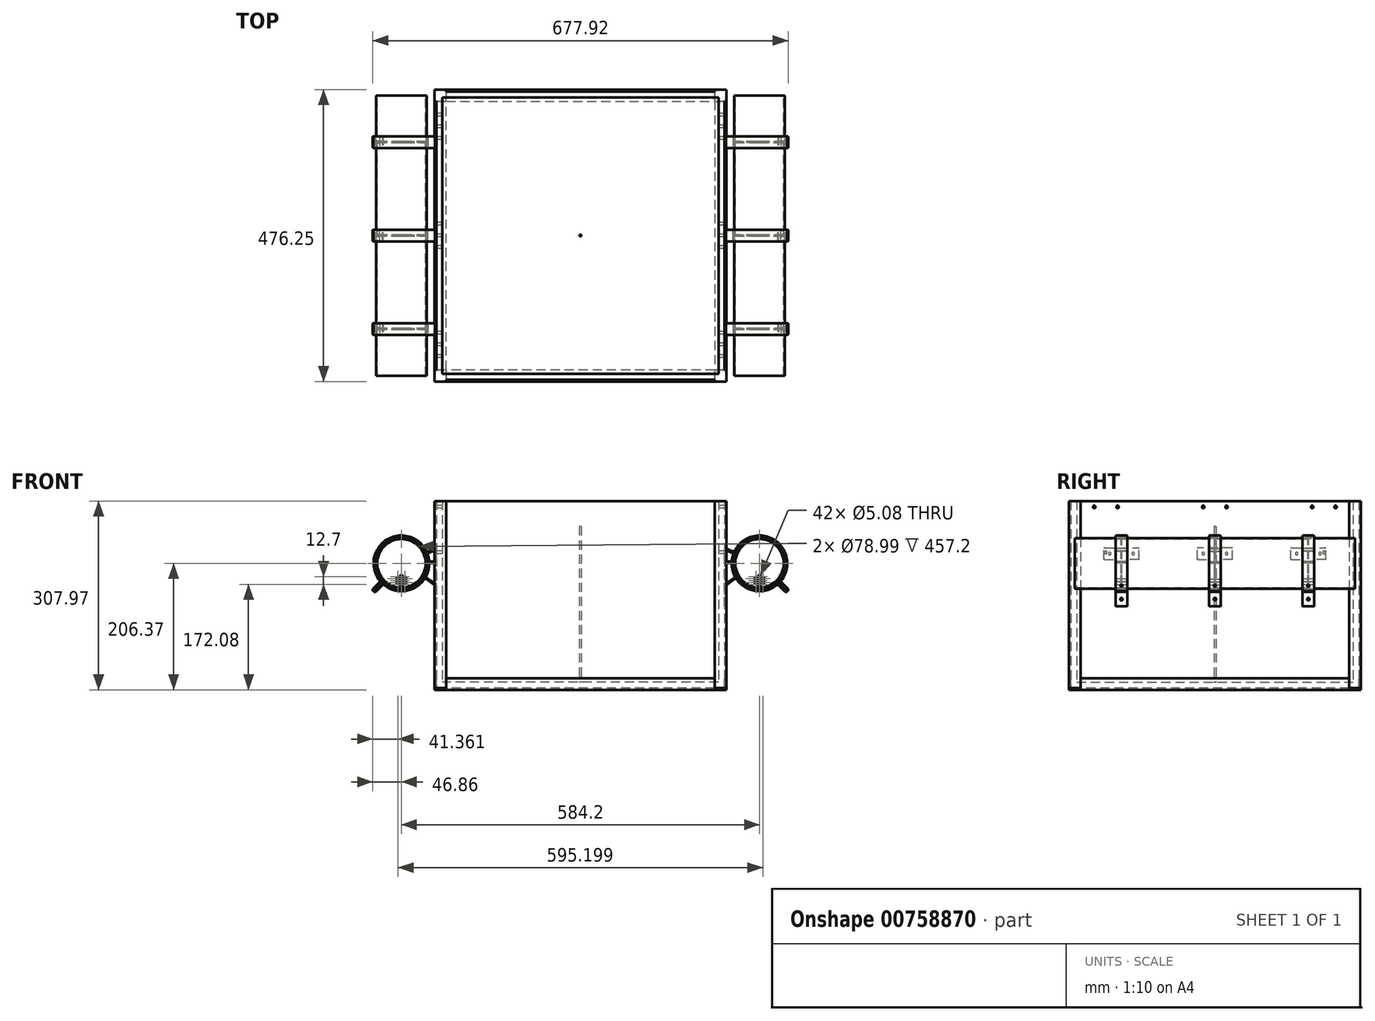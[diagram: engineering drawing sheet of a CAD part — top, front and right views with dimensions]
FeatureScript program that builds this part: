
annotation { "Feature Type Name" : "Feature", "Feature Type Description" : "" }
export const myFeature = defineFeature(function(context is Context, id is Id, definition is map)
    precondition{}
    {
        {
            var Q0;
            Q0=qCreatedBy(makeId("Top.planeOp"),FACE);
            var sketch = newSketch(context, id + "F0", { "sketchPlane" : qUnion([Q0])});
            skLineSegment(sketch, "E0.bottom", {"start": v(234.95, -234.95) * mm, "end": v(-234.95, -234.95) * mm});
            skLineSegment(sketch, "E0.top", {"start": v(234.95, 234.95) * mm, "end": v(-234.95, 234.95) * mm});
            skLineSegment(sketch, "E0.left", {"start": v(234.95, -234.95) * mm, "end": v(234.95, 234.95) * mm});
            skLineSegment(sketch, "E0.right", {"start": v(-234.95, -234.95) * mm, "end": v(-234.95, 234.95) * mm});
            skPoint(sketch, "E0.middle", {"position": v(0, 0) * mm});
            skLineSegment(sketch, "E1", {"start": v(-234.95, 238.13) * mm, "end": v(-238.13, 238.13) * mm});
            skLineSegment(sketch, "E2", {"start": v(-238.13, 238.13) * mm, "end": v(-238.13, 219.08) * mm});
            skLineSegment(sketch, "E3", {"start": v(-238.13, 219.08) * mm, "end": v(-234.95, 219.08) * mm});
            skLineSegment(sketch, "E4", {"start": v(-238.13, 238.13) * mm, "end": v(-219.08, 238.13) * mm});
            skLineSegment(sketch, "E5", {"start": v(-219.08, 238.13) * mm, "end": v(-219.08, 234.95) * mm});
            skLineSegment(sketch, "E6.1.0", {"start": v(-238.13, -238.13) * mm, "end": v(-238.13, -219.08) * mm});
            skLineSegment(sketch, "E6.1.1", {"start": v(-238.13, -238.13) * mm, "end": v(-219.08, -238.13) * mm});
            skLineSegment(sketch, "E6.1.2", {"start": v(-219.08, -238.13) * mm, "end": v(-219.08, -234.95) * mm});
            skLineSegment(sketch, "E6.1.3", {"start": v(-238.13, -219.08) * mm, "end": v(-234.95, -219.08) * mm});
            skLineSegment(sketch, "E6.1.4", {"start": v(-238.13, -234.95) * mm, "end": v(-238.13, -238.13) * mm});
            skLineSegment(sketch, "E6.2.0", {"start": v(238.13, -238.13) * mm, "end": v(219.08, -238.13) * mm});
            skLineSegment(sketch, "E6.2.1", {"start": v(238.13, -238.13) * mm, "end": v(238.13, -219.08) * mm});
            skLineSegment(sketch, "E6.2.2", {"start": v(238.13, -219.08) * mm, "end": v(234.95, -219.08) * mm});
            skLineSegment(sketch, "E6.2.3", {"start": v(219.08, -238.13) * mm, "end": v(219.08, -234.95) * mm});
            skLineSegment(sketch, "E6.2.4", {"start": v(234.95, -238.13) * mm, "end": v(238.13, -238.13) * mm});
            skLineSegment(sketch, "E6.3.0", {"start": v(238.13, 238.13) * mm, "end": v(238.13, 219.08) * mm});
            skLineSegment(sketch, "E6.3.1", {"start": v(238.13, 238.13) * mm, "end": v(219.08, 238.13) * mm});
            skLineSegment(sketch, "E6.3.2", {"start": v(219.08, 238.13) * mm, "end": v(219.08, 234.95) * mm});
            skLineSegment(sketch, "E6.3.3", {"start": v(238.13, 219.08) * mm, "end": v(234.95, 219.08) * mm});
            skLineSegment(sketch, "E6.3.4", {"start": v(238.13, 234.95) * mm, "end": v(238.13, 238.13) * mm});
            skLineSegment(sketch, "E7.0", {"start": v(225.43, 225.43) * mm, "end": v(-225.42, 225.42) * mm});
            skLineSegment(sketch, "E7.1", {"start": v(225.43, -225.42) * mm, "end": v(225.43, 225.42) * mm});
            skLineSegment(sketch, "E7.2", {"start": v(225.43, -225.42) * mm, "end": v(-225.43, -225.43) * mm});
            skLineSegment(sketch, "E7.3", {"start": v(-225.43, -225.43) * mm, "end": v(-225.42, 225.42) * mm});
            skSolve(sketch);
        }
        {
            var Q0;
            Q0=qSketchRegion(id+"F0",true);
            extrude(context, id + "F1", {"entities" : qUnion([Q0]), "depth" : 304.8 * mm, "offsetDistance" : 25.4 * mm});
        }
        {
            var Q0;
            Q0=makeQuery(id+"F0.imprint","IMPRINT",FACE,{"disambiguationData":[TD([[makeQuery(id+"F0.imprint","IMPRINT",EDGE,{"derivedFrom":sQuery(id+"F0.wireOp",EDGE,"E7.0")}),1.0]])]});
            extrude(context, id + "F2", {"entities" : qUnion([Q0]), "operationType" : NewBodyOperationType.ADD, "depth" : 9.52 * mm, "offsetDistance" : 25.4 * mm});
        }
        {
            var Q0;
            Q0=makeQuery(id+"F1.opExtrude","SWEPT_FACE",FACE,{"disambiguationData":[OSD([sQuery(id+"F0.wireOp",EDGE,"E0.right")])]});
            var sketch = newSketch(context, id + "F3", { "sketchPlane" : qUnion([Q0])});
            skLineSegment(sketch, "E8", {"start": v(0, 304.8) * mm, "end": v(0, 297.18) * mm});
            skLineSegment(sketch, "E9", {"start": v(0, 304.8) * mm, "end": v(-177.8, 304.8) * mm});
            skLineSegment(sketch, "E10", {"start": v(-177.8, 304.8) * mm, "end": v(-177.8, 297.18) * mm});
            skLineSegment(sketch, "E11", {"start": v(0, 297.18) * mm, "end": v(0, 220.98) * mm});
            skLineSegment(sketch, "E12", {"start": v(-177.8, 297.18) * mm, "end": v(-177.8, 220.98) * mm});
            skLineSegment(sketch, "E13.MirrorCS", {"start": v(177.8, 304.8) * mm, "end": v(177.8, 297.18) * mm});
            skLineSegment(sketch, "E14.MirrorCS", {"start": v(177.8, 297.18) * mm, "end": v(177.8, 220.98) * mm});
            skLineSegment(sketch, "E15.MirrorCS", {"start": v(0, 304.8) * mm, "end": v(177.8, 304.8) * mm});
            skLineSegment(sketch, "E16", {"start": v(-177.8, 304.8) * mm, "end": v(-177.8, 295.28) * mm});
            skLineSegment(sketch, "E17", {"start": v(-177.8, 295.28) * mm, "end": v(-158.75, 295.28) * mm});
            skLineSegment(sketch, "E18.MirrorCS", {"start": v(-177.8, 295.28) * mm, "end": v(-196.85, 295.28) * mm});
            skLineSegment(sketch, "E19", {"start": v(-88.9, 304.8) * mm, "end": v(-88.9, 246.4) * mm});
            skLineSegment(sketch, "E20.MirrorCS", {"start": v(0, 304.8) * mm, "end": v(0, 295.28) * mm});
            skLineSegment(sketch, "E21.MirrorCS", {"start": v(0, 295.28) * mm, "end": v(19.05, 295.28) * mm});
            skLineSegment(sketch, "E22.MirrorCS", {"start": v(0, 295.28) * mm, "end": v(-19.05, 295.28) * mm});
            skLineSegment(sketch, "E23.MirrorCS", {"start": v(177.8, 304.8) * mm, "end": v(177.8, 295.28) * mm});
            skLineSegment(sketch, "E24.MirrorCS", {"start": v(177.8, 295.28) * mm, "end": v(196.85, 295.28) * mm});
            skLineSegment(sketch, "E25.MirrorCS", {"start": v(177.8, 295.28) * mm, "end": v(158.75, 295.28) * mm});
            skSolve(sketch);
        }
        {
            var Q0;
            Q0=sQuery(id+"F3.wireOp",VERTEX,"E11.end");
            var Q1;
            Q1=sQuery(id+"F3.wireOp",VERTEX,"E14.MirrorCS.end");
            var Q2;
            Q2=sQuery(id+"F3.wireOp",VERTEX,"E17.end");
            var Q3;
            Q3=sQuery(id+"F3.wireOp",VERTEX,"E18.MirrorCS.end");
            var Q4;
            Q4=sQuery(id+"F3.wireOp",VERTEX,"E22.MirrorCS.end");
            var Q5;
            Q5=sQuery(id+"F3.wireOp",VERTEX,"E21.MirrorCS.end");
            var Q6;
            Q6=sQuery(id+"F3.wireOp",VERTEX,"E12.end");
            var Q7;
            Q7=sQuery(id+"F3.wireOp",VERTEX,"E24.MirrorCS.end");
            var Q8;
            Q8=sQuery(id+"F3.wireOp",VERTEX,"E25.MirrorCS.end");
            var Q9;
            Q9=makeQuery(id+"F1.opExtrude","SWEPT_BODY",BODY,{"disambiguationData":[OSD([sQuery(id+"F0.wireOp",EDGE,"E0.bottom"),sQuery(id+"F0.wireOp",EDGE,"E0.top"),sQuery(id+"F0.wireOp",EDGE,"E0.left"),sQuery(id+"F0.wireOp",EDGE,"E0.right"),sQuery(id+"F0.wireOp",EDGE,"E2"),sQuery(id+"F0.wireOp",EDGE,"E3"),sQuery(id+"F0.wireOp",EDGE,"E4"),sQuery(id+"F0.wireOp",EDGE,"E5"),sQuery(id+"F0.wireOp",EDGE,"E6.1.0"),sQuery(id+"F0.wireOp",EDGE,"E6.1.1"),sQuery(id+"F0.wireOp",EDGE,"E6.1.2"),sQuery(id+"F0.wireOp",EDGE,"E6.1.3"),sQuery(id+"F0.wireOp",EDGE,"E6.1.4"),sQuery(id+"F0.wireOp",EDGE,"E6.2.0"),sQuery(id+"F0.wireOp",EDGE,"E6.2.1"),sQuery(id+"F0.wireOp",EDGE,"E6.2.2"),sQuery(id+"F0.wireOp",EDGE,"E6.2.3"),sQuery(id+"F0.wireOp",EDGE,"E6.2.4"),sQuery(id+"F0.wireOp",EDGE,"E6.3.0"),sQuery(id+"F0.wireOp",EDGE,"E6.3.1"),sQuery(id+"F0.wireOp",EDGE,"E6.3.2"),sQuery(id+"F0.wireOp",EDGE,"E6.3.3"),sQuery(id+"F0.wireOp",EDGE,"E6.3.4"),sQuery(id+"F0.wireOp",EDGE,"E7.0"),sQuery(id+"F0.wireOp",EDGE,"E7.1"),sQuery(id+"F0.wireOp",EDGE,"E7.2"),sQuery(id+"F0.wireOp",EDGE,"E7.3")])]});
            hole(context, id + "F4", {"style" : HoleStyle.SIMPLE, "endStyle" : HoleEndStyle.BLIND, "standardTappedOrClearance" : lookupTablePath({ "standard" : "ANSI", "fit" : "Close", "size" : "#8", "type" : "Clearance" }), "standardBlindInLast" : lookupTablePath({ "fit" : "Close", "standard" : "ANSI", "size" : "#8", "type" : "Clearance" }), "holeDiameter" : 4.32 * mm, "holeDepth" : 762 * mm, "isTappedThrough" : true, "tappedDepth" : 12.7 * mm, "tapClearance" : 3, "locations" : qUnion([Q0, Q1, Q2, Q3, Q4, Q5, Q6, Q7, Q8]), "scope" : qUnion([Q9]), "majorDiameter" : 6.35 * mm});
        }
        {
            var Q0;
            Q0=makeQuery(id+"F1.opExtrude","SWEPT_FACE",FACE,{"disambiguationData":[OSD([sQuery(id+"F0.wireOp",EDGE,"E6.1.2")])]});
            var sketch = newSketch(context, id + "F5", { "sketchPlane" : qUnion([Q0])});
            skLineSegment(sketch, "E26", {"start": v(-238.12, -3.17) * mm, "end": v(-238.12, 15.87) * mm});
            skLineSegment(sketch, "E27", {"start": v(-238.12, 15.87) * mm, "end": v(-234.95, 15.87) * mm});
            skLineSegment(sketch, "E28", {"start": v(-234.95, 15.87) * mm, "end": v(-234.95, 0) * mm});
            skLineSegment(sketch, "E29", {"start": v(-234.95, 0) * mm, "end": v(-219.07, 0) * mm});
            skLineSegment(sketch, "E30", {"start": v(-219.07, 0) * mm, "end": v(-219.07, -3.17) * mm});
            skLineSegment(sketch, "E31", {"start": v(-219.07, -3.17) * mm, "end": v(-238.12, -3.17) * mm});
            skSolve(sketch);
        }
        {
            var Q0;
            Q0=qSketchRegion(id+"F5",true);
            var Q1;
            Q1=makeQuery(id+"F1.opExtrude","SWEPT_FACE",FACE,{"disambiguationData":[OSD([sQuery(id+"F0.wireOp",EDGE,"E6.2.3")])]});
            extrude(context, id + "F6", {"entities" : qUnion([Q0]), "endBound" : BoundingType.UP_TO_SURFACE, "depth" : 25.4 * mm, "endBoundEntityFace" : qUnion([Q1]), "offsetDistance" : 25.4 * mm});
        }
        {
            var Q0;
            Q0=makeQuery(id+"F2.opExtrude","CAP_FACE",FACE,{"disambiguationData":[OSD([sQuery(id+"F0.wireOp",EDGE,"E7.0"),sQuery(id+"F0.wireOp",EDGE,"E7.1"),sQuery(id+"F0.wireOp",EDGE,"E7.2"),sQuery(id+"F0.wireOp",EDGE,"E7.3")])],"isStart":false});
            var sketch = newSketch(context, id + "F7", { "sketchPlane" : qUnion([Q0])});
            skCircle(sketch, "E32", {"center": v(0, 0) * mm, "radius": 1.59 * mm});
            skSolve(sketch);
        }
        {
            var Q0;
            Q0=qSketchRegion(id+"F7",true);
            extrude(context, id + "F8", {"entities" : qUnion([Q0]), "operationType" : NewBodyOperationType.ADD, "depth" : 254 * mm, "offsetDistance" : 25.4 * mm});
        }
        {
            var Q0;
            Q0=makeQuery(id+"F6.opExtrude","SWEPT_BODY",BODY,{"disambiguationData":[OSD([sQuery(id+"F5.wireOp",EDGE,"E26"),sQuery(id+"F5.wireOp",EDGE,"E27"),sQuery(id+"F5.wireOp",EDGE,"E28"),sQuery(id+"F5.wireOp",EDGE,"E29"),sQuery(id+"F5.wireOp",EDGE,"E30"),sQuery(id+"F5.wireOp",EDGE,"E31")])]});
            var Q1;
            Q1=makeQuery(id+"F8.opExtrude","SWEPT_FACE",FACE,{"disambiguationData":[OSD([sQuery(id+"F7.wireOp",EDGE,"E32")])]});
            circularPattern(context, id + "F9", {"entities" : qUnion([Q0]), "axis" : qUnion([Q1]), "angle" : 360 * degree, "instanceCount" : 4, "equalSpace" : true});
        }
        {
            var Q0;
            Q0=qCreatedBy(makeId("Front.planeOp"),FACE);
            var sketch = newSketch(context, id + "F10", { "sketchPlane" : qUnion([Q0])});
            skLineSegment(sketch, "E33", {"start": v(0, 0) * mm, "end": v(0, 279.4) * mm});
            skLineSegment(sketch, "E34", {"start": v(0, 279.4) * mm, "end": v(238.13, 279.4) * mm});
            skCircle(sketch, "E35", {"center": v(292.1, 279.4) * mm, "radius": 41.28 * mm});
            skCircle(sketch, "E36", {"center": v(292.1, 279.4) * mm, "radius": 39.5 * mm});
            skLineSegment(sketch, "E37", {"start": v(292.1, 279.4) * mm, "end": v(250.83, 279.4) * mm});
            skLineSegment(sketch, "E38", {"start": v(250.83, 279.4) * mm, "end": v(238.13, 279.4) * mm});
            skSolve(sketch);
        }
        {
            var Q0;
            Q0=qSketchRegion(id+"F10",true);
            extrude(context, id + "F11", {"entities" : qUnion([Q0]), "endBound" : BoundingType.SYMMETRIC, "depth" : 457.2 * mm, "offsetDistance" : 25.4 * mm});
        }
        {
            var Q0;
            Q0=qCreatedBy(makeId("Front.planeOp"),FACE);
            var sketch = newSketch(context, id + "F12", { "sketchPlane" : qUnion([Q0])});
            skLineSegment(sketch, "E39", {"start": v(0, 0) * mm, "end": v(0, 40.83) * mm});
            skLineSegment(sketch, "E40", {"start": v(248.33, 298.8) * mm, "end": v(237.5, 303.6) * mm});
            skLineSegment(sketch, "E41", {"start": v(237.5, 209.55) * mm, "end": v(234.95, 209.55) * mm});
            skLineSegment(sketch, "E42", {"start": v(251.7, 253.53) * mm, "end": v(238.58, 244.41) * mm});
            skArc(sketch, "E43.0", {"start": v(322.94, 249.64) * mm, "mid": v(261.8, 309.7) * mm, "end": v(321.86, 248.56) * mm});
            skArc(sketch, "E44.0", {"start": v(246.75, 277.28) * mm, "mid": v(248.16, 267.95) * mm, "end": v(251.48, 259.12) * mm});
            skLineSegment(sketch, "E45", {"start": v(244.2, 279.7) * mm, "end": v(240.03, 279.7) * mm});
            skLineSegment(sketch, "E46.0", {"start": v(244.46, 282.24) * mm, "end": v(240.03, 282.24) * mm});
            skLineSegment(sketch, "E47.trimOffspring", {"start": v(237.5, 296.8) * mm, "end": v(237.5, 284.78) * mm});
            skLineSegment(sketch, "E48.trimOffspring", {"start": v(247.46, 296.1) * mm, "end": v(241.11, 299.1) * mm});
            skLineSegment(sketch, "E49.trimOffspring", {"start": v(237.5, 277.16) * mm, "end": v(237.5, 251.6) * mm});
            skArc(sketch, "E50.trimOffspring", {"start": v(255.22, 252.93) * mm, "mid": v(285.65, 234.46) * mm, "end": v(320.05, 243.62) * mm});
            skLineSegment(sketch, "E51.trimOffspring", {"start": v(250.66, 255.9) * mm, "end": v(241.48, 249.52) * mm});
            skLineSegment(sketch, "E52.trimOffspring", {"start": v(237.5, 242.33) * mm, "end": v(237.5, 209.55) * mm});
            skArc(sketch, "E53.trimOffspring", {"start": v(248.8, 293.05) * mm, "mid": v(247.68, 288.82) * mm, "end": v(246.98, 284.5) * mm});
            skLineSegment(sketch, "E54", {"start": v(292.1, 279.4) * mm, "end": v(292.1, 252.05) * mm});
            skLineSegment(sketch, "E55", {"start": v(292.1, 279.4) * mm, "end": v(324.2, 247.3) * mm});
            skLineSegment(sketch, "E56", {"start": v(324.2, 247.3) * mm, "end": v(337.67, 233.83) * mm});
            skLineSegment(sketch, "E57.0", {"start": v(323.66, 246.76) * mm, "end": v(337.14, 233.28) * mm});
            skLineSegment(sketch, "E58.0", {"start": v(324.74, 247.84) * mm, "end": v(338.22, 234.36) * mm});
            skArc(sketch, "E59.trimOffspring", {"start": v(327.88, 251.45) * mm, "mid": v(316.48, 317.7) * mm, "end": v(251.62, 299.97) * mm});
            skLineSegment(sketch, "E60", {"start": v(323.66, 246.76) * mm, "end": v(321.86, 248.56) * mm});
            skLineSegment(sketch, "E61", {"start": v(324.74, 247.84) * mm, "end": v(322.94, 249.64) * mm});
            skLineSegment(sketch, "E62", {"start": v(337.14, 233.28) * mm, "end": v(337.14, 233.28) * mm});
            skLineSegment(sketch, "E63", {"start": v(333.55, 233.28) * mm, "end": v(323.41, 243.42) * mm});
            skLineSegment(sketch, "E64.MirrorCS", {"start": v(338.22, 237.95) * mm, "end": v(328.08, 248.09) * mm});
            skLineSegment(sketch, "E65.MirrorCS", {"start": v(338.22, 234.36) * mm, "end": v(338.22, 234.36) * mm});
            skPoint(sketch, "E66.visualSharp", {"position": v(250.6, 297.8) * mm});
            skArc(sketch, "E66.filletArc", {"start": v(248.33, 298.8) * mm, "mid": v(250.21, 298.73) * mm, "end": v(251.62, 299.97) * mm});
            skPoint(sketch, "E67.visualSharp", {"position": v(249.51, 295.14) * mm});
            skArc(sketch, "E67.filletArc", {"start": v(248.8, 293.05) * mm, "mid": v(248.7, 294.83) * mm, "end": v(247.46, 296.1) * mm});
            skPoint(sketch, "E68.visualSharp", {"position": v(237.5, 300.8) * mm});
            skArc(sketch, "E68.filletArc", {"start": v(241.11, 299.1) * mm, "mid": v(238.67, 298.94) * mm, "end": v(237.5, 296.8) * mm});
            skPoint(sketch, "E69.visualSharp", {"position": v(246.79, 282.24) * mm});
            skArc(sketch, "E69.filletArc", {"start": v(244.46, 282.24) * mm, "mid": v(246.15, 282.89) * mm, "end": v(246.98, 284.5) * mm});
            skPoint(sketch, "E70.visualSharp", {"position": v(237.5, 282.24) * mm});
            skArc(sketch, "E70.filletArc", {"start": v(237.5, 284.78) * mm, "mid": v(238.23, 282.99) * mm, "end": v(240.03, 282.24) * mm});
            skPoint(sketch, "E71.visualSharp", {"position": v(237.5, 279.7) * mm});
            skArc(sketch, "E71.filletArc", {"start": v(240.03, 279.7) * mm, "mid": v(238.23, 278.96) * mm, "end": v(237.5, 277.16) * mm});
            skPoint(sketch, "E72.visualSharp", {"position": v(246.7, 279.7) * mm});
            skArc(sketch, "E72.filletArc", {"start": v(246.75, 277.28) * mm, "mid": v(245.96, 279) * mm, "end": v(244.2, 279.7) * mm});
            skPoint(sketch, "E73.visualSharp", {"position": v(252.5, 257.18) * mm});
            skArc(sketch, "E73.filletArc", {"start": v(250.66, 255.9) * mm, "mid": v(251.67, 257.35) * mm, "end": v(251.48, 259.12) * mm});
            skPoint(sketch, "E74.visualSharp", {"position": v(237.5, 246.75) * mm});
            skArc(sketch, "E74.filletArc", {"start": v(237.5, 251.6) * mm, "mid": v(238.85, 249.35) * mm, "end": v(241.48, 249.52) * mm});
            skPoint(sketch, "E75.visualSharp", {"position": v(237.5, 243.65) * mm});
            skArc(sketch, "E75.filletArc", {"start": v(238.58, 244.41) * mm, "mid": v(237.78, 243.5) * mm, "end": v(237.5, 242.33) * mm});
            skPoint(sketch, "E76.visualSharp", {"position": v(253.81, 255) * mm});
            skArc(sketch, "E76.filletArc", {"start": v(255.22, 252.93) * mm, "mid": v(253.58, 253.95) * mm, "end": v(251.7, 253.53) * mm});
            skPoint(sketch, "E77.visualSharp", {"position": v(321.78, 245.05) * mm});
            skArc(sketch, "E77.filletArc", {"start": v(323.41, 243.42) * mm, "mid": v(321.77, 244.16) * mm, "end": v(320.05, 243.62) * mm});
            skPoint(sketch, "E78.visualSharp", {"position": v(326.45, 249.72) * mm});
            skArc(sketch, "E78.filletArc", {"start": v(327.88, 251.45) * mm, "mid": v(327.34, 249.73) * mm, "end": v(328.08, 248.09) * mm});
            skPoint(sketch, "E79.visualSharp", {"position": v(340.01, 236.16) * mm});
            skArc(sketch, "E79.filletArc", {"start": v(338.22, 234.36) * mm, "mid": v(338.96, 236.16) * mm, "end": v(338.22, 237.95) * mm});
            skPoint(sketch, "E80.visualSharp", {"position": v(335.34, 231.49) * mm});
            skArc(sketch, "E80.filletArc", {"start": v(333.55, 233.28) * mm, "mid": v(335.34, 232.54) * mm, "end": v(337.14, 233.28) * mm});
            skPoint(sketch, "E81.visualSharp", {"position": v(237.5, 304.8) * mm});
            skLineSegment(sketch, "E82", {"start": v(237.5, 303.6) * mm, "end": v(237.5, 304.8) * mm});
            skLineSegment(sketch, "E83", {"start": v(234.95, 304.8) * mm, "end": v(237.5, 304.8) * mm});
            skLineSegment(sketch, "E84", {"start": v(234.95, 209.55) * mm, "end": v(234.95, 304.8) * mm});
            skSolve(sketch);
        }
        {
            var Q0;
            Q0=qSketchRegion(id+"F12",true);
            extrude(context, id + "F13", {"entities" : qUnion([Q0]), "endBound" : BoundingType.SYMMETRIC, "depth" : 19.05 * mm, "offsetDistance" : 25.4 * mm});
        }
        {
            var Q0;
            Q0=makeQuery(id+"F13.opExtrude","SWEPT_FACE",FACE,{"disambiguationData":[OSD([sQuery(id+"F12.wireOp",EDGE,"E64.MirrorCS")])]});
            var sketch = newSketch(context, id + "F14", { "sketchPlane" : qUnion([Q0])});
            skLineSegment(sketch, "E85", {"start": v(-9.53, -56.57) * mm, "end": v(9.53, -70.9) * mm});
            skLineSegment(sketch, "E86", {"start": v(9.53, -56.57) * mm, "end": v(-9.53, -70.9) * mm});
            skLineSegment(sketch, "E87", {"start": v(-9.53, -70.9) * mm, "end": v(0, -63.73) * mm});
            skLineSegment(sketch, "E88", {"start": v(0, -63.73) * mm, "end": v(0, -59.85) * mm});
            skSolve(sketch);
        }
        {
            var Q0;
            Q0=sQuery(id+"F14.wireOp",VERTEX,"E88.start");
            var Q1;
            Q1=makeQuery(id+"F13.opExtrude","SWEPT_BODY",BODY,{"disambiguationData":[OSD([sQuery(id+"F12.wireOp",EDGE,"E40"),sQuery(id+"F12.wireOp",EDGE,"XVp6BJce-8Tfc-asBP-cGqg-N5JEgT9na927"),sQuery(id+"F12.wireOp",EDGE,"cfrEHy57-AOKR-8SEr-zHKb-8GyFvIi9nsPC"),sQuery(id+"F12.wireOp",EDGE,"E41"),sQuery(id+"F12.wireOp",EDGE,"E42"),sQuery(id+"F12.wireOp",EDGE,"E43.0"),sQuery(id+"F12.wireOp",EDGE,"E44.0"),sQuery(id+"F12.wireOp",EDGE,"E45"),sQuery(id+"F12.wireOp",EDGE,"E46.0"),sQuery(id+"F12.wireOp",EDGE,"E47.trimOffspring"),sQuery(id+"F12.wireOp",EDGE,"E48.trimOffspring"),sQuery(id+"F12.wireOp",EDGE,"E49.trimOffspring"),sQuery(id+"F12.wireOp",EDGE,"E50.trimOffspring"),sQuery(id+"F12.wireOp",EDGE,"E51.trimOffspring"),sQuery(id+"F12.wireOp",EDGE,"E52.trimOffspring"),sQuery(id+"F12.wireOp",EDGE,"E53.trimOffspring"),sQuery(id+"F12.wireOp",EDGE,"E57.0"),sQuery(id+"F12.wireOp",EDGE,"E58.0"),sQuery(id+"F12.wireOp",EDGE,"E59.trimOffspring"),sQuery(id+"F12.wireOp",EDGE,"E60"),sQuery(id+"F12.wireOp",EDGE,"E61"),sQuery(id+"F12.wireOp",EDGE,"E63"),sQuery(id+"F12.wireOp",EDGE,"E64.MirrorCS"),sQuery(id+"F12.wireOp",EDGE,"E66.filletArc"),sQuery(id+"F12.wireOp",EDGE,"E67.filletArc"),sQuery(id+"F12.wireOp",EDGE,"E68.filletArc"),sQuery(id+"F12.wireOp",EDGE,"E69.filletArc"),sQuery(id+"F12.wireOp",EDGE,"E70.filletArc"),sQuery(id+"F12.wireOp",EDGE,"E71.filletArc"),sQuery(id+"F12.wireOp",EDGE,"E72.filletArc"),sQuery(id+"F12.wireOp",EDGE,"E73.filletArc"),sQuery(id+"F12.wireOp",EDGE,"E74.filletArc"),sQuery(id+"F12.wireOp",EDGE,"E75.filletArc"),sQuery(id+"F12.wireOp",EDGE,"E76.filletArc"),sQuery(id+"F12.wireOp",EDGE,"E77.filletArc"),sQuery(id+"F12.wireOp",EDGE,"E78.filletArc"),sQuery(id+"F12.wireOp",EDGE,"E79.filletArc"),sQuery(id+"F12.wireOp",EDGE,"E80.filletArc"),sQuery(id+"F12.wireOp",EDGE,"E81.filletArc"),sQuery(id+"F12.wireOp",EDGE,"QRnfTjK7-z6Yt-K2ef-ZXCt-E60ytMqK47gu")])]});
            hole(context, id + "F15", {"style" : HoleStyle.SIMPLE, "endStyle" : HoleEndStyle.BLIND, "standardTappedOrClearance" : lookupTablePath({ "standard" : "ANSI", "fit" : "Close", "size" : "#6", "type" : "Clearance" }), "standardBlindInLast" : lookupTablePath({ "fit" : "Close", "standard" : "ANSI", "size" : "#6", "type" : "Clearance" }), "holeDiameter" : 3.66 * mm, "majorDiameter" : 6.35 * mm, "holeDepth" : 25.4 * mm, "isTappedThrough" : true, "tappedDepth" : 12.7 * mm, "tapClearance" : 3, "locations" : qUnion([Q0]), "scope" : qUnion([Q1])});
        }
        {
            var Q0;
            Q0=makeQuery(id+"F13.opExtrude","CAP_FACE",FACE,{"disambiguationData":[OSD([sQuery(id+"F12.wireOp",EDGE,"E40"),sQuery(id+"F12.wireOp",EDGE,"E41"),sQuery(id+"F12.wireOp",EDGE,"E42"),sQuery(id+"F12.wireOp",EDGE,"E43.0"),sQuery(id+"F12.wireOp",EDGE,"E44.0"),sQuery(id+"F12.wireOp",EDGE,"E45"),sQuery(id+"F12.wireOp",EDGE,"E46.0"),sQuery(id+"F12.wireOp",EDGE,"E47.trimOffspring"),sQuery(id+"F12.wireOp",EDGE,"E48.trimOffspring"),sQuery(id+"F12.wireOp",EDGE,"E49.trimOffspring"),sQuery(id+"F12.wireOp",EDGE,"E50.trimOffspring"),sQuery(id+"F12.wireOp",EDGE,"E51.trimOffspring"),sQuery(id+"F12.wireOp",EDGE,"E52.trimOffspring"),sQuery(id+"F12.wireOp",EDGE,"E53.trimOffspring"),sQuery(id+"F12.wireOp",EDGE,"E57.0"),sQuery(id+"F12.wireOp",EDGE,"E58.0"),sQuery(id+"F12.wireOp",EDGE,"E59.trimOffspring"),sQuery(id+"F12.wireOp",EDGE,"E60"),sQuery(id+"F12.wireOp",EDGE,"E61"),sQuery(id+"F12.wireOp",EDGE,"E63"),sQuery(id+"F12.wireOp",EDGE,"E64.MirrorCS"),sQuery(id+"F12.wireOp",EDGE,"E66.filletArc"),sQuery(id+"F12.wireOp",EDGE,"E67.filletArc"),sQuery(id+"F12.wireOp",EDGE,"E68.filletArc"),sQuery(id+"F12.wireOp",EDGE,"E69.filletArc"),sQuery(id+"F12.wireOp",EDGE,"E70.filletArc"),sQuery(id+"F12.wireOp",EDGE,"E71.filletArc"),sQuery(id+"F12.wireOp",EDGE,"E72.filletArc"),sQuery(id+"F12.wireOp",EDGE,"E73.filletArc"),sQuery(id+"F12.wireOp",EDGE,"E74.filletArc"),sQuery(id+"F12.wireOp",EDGE,"E75.filletArc"),sQuery(id+"F12.wireOp",EDGE,"E76.filletArc"),sQuery(id+"F12.wireOp",EDGE,"E77.filletArc"),sQuery(id+"F12.wireOp",EDGE,"E78.filletArc"),sQuery(id+"F12.wireOp",EDGE,"E79.filletArc"),sQuery(id+"F12.wireOp",EDGE,"E80.filletArc"),sQuery(id+"F12.wireOp",EDGE,"E82"),sQuery(id+"F12.wireOp",EDGE,"E83"),sQuery(id+"F12.wireOp",EDGE,"E84")])],"isStart":false});
            var sketch = newSketch(context, id + "F16", { "sketchPlane" : qUnion([Q0])});
            skLineSegment(sketch, "E89", {"start": v(234.95, 304.8) * mm, "end": v(237.5, 304.8) * mm});
            skLineSegment(sketch, "E90", {"start": v(237.5, 304.8) * mm, "end": v(237.5, 285.75) * mm});
            skLineSegment(sketch, "E91", {"start": v(237.5, 285.75) * mm, "end": v(234.95, 285.75) * mm});
            skLineSegment(sketch, "E92", {"start": v(234.95, 285.75) * mm, "end": v(234.95, 304.8) * mm});
            skSolve(sketch);
        }
        {
            var Q0;
            Q0=qSketchRegion(id+"F16",true);
            extrude(context, id + "F17", {"entities" : qUnion([Q0]), "depth" : 19.05 * mm, "offsetDistance" : 25.4 * mm});
        }
        {
            var Q0;
            Q0=makeQuery(id+"F17.opExtrude","SWEPT_BODY",BODY,{"disambiguationData":[OSD([sQuery(id+"F16.wireOp",EDGE,"E89"),sQuery(id+"F16.wireOp",EDGE,"E90"),sQuery(id+"F16.wireOp",EDGE,"E91"),sQuery(id+"F16.wireOp",EDGE,"E92")])]});
            var Q1;
            Q1=qCreatedBy(makeId("Front.planeOp"),FACE);
            mirror(context, id + "F18", {"entities" : qUnion([Q0]), "mirrorPlane" : qUnion([Q1])});
        }
        {
            var Q0;
            Q0=makeQuery(id+"F18.opPattern","COPY",BODY,{"derivedFrom":makeQuery(id+"F17.opExtrude","SWEPT_BODY",BODY,{"disambiguationData":[OSD([sQuery(id+"F16.wireOp",EDGE,"E89"),sQuery(id+"F16.wireOp",EDGE,"E90"),sQuery(id+"F16.wireOp",EDGE,"E91"),sQuery(id+"F16.wireOp",EDGE,"E92")])]}),"instanceName":"1"});
            var Q1;
            Q1=makeQuery(id+"F17.opExtrude","SWEPT_BODY",BODY,{"disambiguationData":[OSD([sQuery(id+"F16.wireOp",EDGE,"E89"),sQuery(id+"F16.wireOp",EDGE,"E90"),sQuery(id+"F16.wireOp",EDGE,"E91"),sQuery(id+"F16.wireOp",EDGE,"E92")])]});
            var Q2;
            Q2=makeQuery(id+"F13.opExtrude","SWEPT_BODY",BODY,{"disambiguationData":[OSD([sQuery(id+"F12.wireOp",EDGE,"E40"),sQuery(id+"F12.wireOp",EDGE,"E41"),sQuery(id+"F12.wireOp",EDGE,"E42"),sQuery(id+"F12.wireOp",EDGE,"E43.0"),sQuery(id+"F12.wireOp",EDGE,"E44.0"),sQuery(id+"F12.wireOp",EDGE,"E45"),sQuery(id+"F12.wireOp",EDGE,"E46.0"),sQuery(id+"F12.wireOp",EDGE,"E47.trimOffspring"),sQuery(id+"F12.wireOp",EDGE,"E48.trimOffspring"),sQuery(id+"F12.wireOp",EDGE,"E49.trimOffspring"),sQuery(id+"F12.wireOp",EDGE,"E50.trimOffspring"),sQuery(id+"F12.wireOp",EDGE,"E51.trimOffspring"),sQuery(id+"F12.wireOp",EDGE,"E52.trimOffspring"),sQuery(id+"F12.wireOp",EDGE,"E53.trimOffspring"),sQuery(id+"F12.wireOp",EDGE,"E57.0"),sQuery(id+"F12.wireOp",EDGE,"E58.0"),sQuery(id+"F12.wireOp",EDGE,"E59.trimOffspring"),sQuery(id+"F12.wireOp",EDGE,"E60"),sQuery(id+"F12.wireOp",EDGE,"E61"),sQuery(id+"F12.wireOp",EDGE,"E63"),sQuery(id+"F12.wireOp",EDGE,"E64.MirrorCS"),sQuery(id+"F12.wireOp",EDGE,"E66.filletArc"),sQuery(id+"F12.wireOp",EDGE,"E67.filletArc"),sQuery(id+"F12.wireOp",EDGE,"E68.filletArc"),sQuery(id+"F12.wireOp",EDGE,"E69.filletArc"),sQuery(id+"F12.wireOp",EDGE,"E70.filletArc"),sQuery(id+"F12.wireOp",EDGE,"E71.filletArc"),sQuery(id+"F12.wireOp",EDGE,"E72.filletArc"),sQuery(id+"F12.wireOp",EDGE,"E73.filletArc"),sQuery(id+"F12.wireOp",EDGE,"E74.filletArc"),sQuery(id+"F12.wireOp",EDGE,"E75.filletArc"),sQuery(id+"F12.wireOp",EDGE,"E76.filletArc"),sQuery(id+"F12.wireOp",EDGE,"E77.filletArc"),sQuery(id+"F12.wireOp",EDGE,"E78.filletArc"),sQuery(id+"F12.wireOp",EDGE,"E79.filletArc"),sQuery(id+"F12.wireOp",EDGE,"E80.filletArc"),sQuery(id+"F12.wireOp",EDGE,"E82"),sQuery(id+"F12.wireOp",EDGE,"E83"),sQuery(id+"F12.wireOp",EDGE,"E84")])]});
            booleanBodies(context, id + "F19", {"operationType" : BooleanOperationType.UNION, "tools" : qUnion([Q0, Q1, Q2])});
        }
        {
            var Q0;
            {var subQ0=makeQuery(id+"F17.opExtrude","SWEPT_FACE",FACE,{"disambiguationData":[OSD([sQuery(id+"F16.wireOp",EDGE,"E90")])]});Q0=makeQuery(id+"F19.opBoolean","MERGE",FACE,{"derivedFrom":[makeQuery(id+"F13.opExtrude","SWEPT_FACE",FACE,{"disambiguationData":[OSD([sQuery(id+"F12.wireOp",EDGE,"E47.trimOffspring")])]}),makeQuery(id+"F13.opExtrude","SWEPT_FACE",FACE,{"disambiguationData":[OSD([sQuery(id+"F12.wireOp",EDGE,"E82")])]}),subQ0,makeQuery(id+"F18.opPattern","COPY",FACE,{"derivedFrom":subQ0,"instanceName":"1"})]});}
            var sketch = newSketch(context, id + "F20", { "sketchPlane" : qUnion([Q0])});
            skLineSegment(sketch, "E93", {"start": v(-28.58, 304.8) * mm, "end": v(28.58, 304.8) * mm});
            skLineSegment(sketch, "E94", {"start": v(-28.58, 304.8) * mm, "end": v(-19.05, 304.8) * mm});
            skLineSegment(sketch, "E95", {"start": v(-19.05, 304.8) * mm, "end": v(-19.05, 295.28) * mm});
            skLineSegment(sketch, "E96", {"start": v(0, 304.8) * mm, "end": v(0, 288.55) * mm});
            skLineSegment(sketch, "E97.MirrorCS", {"start": v(28.58, 304.8) * mm, "end": v(19.05, 304.8) * mm});
            skLineSegment(sketch, "E98.MirrorCS", {"start": v(19.05, 304.8) * mm, "end": v(19.05, 295.28) * mm});
            skSolve(sketch);
        }
        {
            var Q0;
            Q0=sQuery(id+"F20.wireOp",VERTEX,"E98.MirrorCS.end");
            var Q1;
            Q1=sQuery(id+"F20.wireOp",VERTEX,"E95.end");
            var Q2;
            Q2=makeQuery(id+"F18.opPattern","COPY",BODY,{"derivedFrom":makeQuery(id+"F17.opExtrude","SWEPT_BODY",BODY,{"disambiguationData":[OSD([sQuery(id+"F16.wireOp",EDGE,"E89"),sQuery(id+"F16.wireOp",EDGE,"E90"),sQuery(id+"F16.wireOp",EDGE,"E91"),sQuery(id+"F16.wireOp",EDGE,"E92")])]}),"instanceName":"1"});
            hole(context, id + "F21", {"style" : HoleStyle.SIMPLE, "endStyle" : HoleEndStyle.THROUGH, "standardTappedOrClearance" : lookupTablePath({ "standard" : "ANSI", "fit" : "Close", "size" : "#8", "type" : "Clearance" }), "standardBlindInLast" : lookupTablePath({ "fit" : "Close", "standard" : "ANSI", "size" : "#8", "type" : "Clearance" }), "holeDiameter" : 4.32 * mm, "majorDiameter" : 6.35 * mm, "isTappedThrough" : true, "tappedDepth" : 12.7 * mm, "tapClearance" : 3, "locations" : qUnion([Q0, Q1]), "scope" : qUnion([Q2])});
        }
        {
            var Q0;
            Q0=makeQuery(id+"F13.opExtrude","SWEPT_FACE",FACE,{"disambiguationData":[OSD([sQuery(id+"F12.wireOp",EDGE,"E52.trimOffspring")])]});
            var sketch = newSketch(context, id + "F22", { "sketchPlane" : qUnion([Q0])});
            skLineSegment(sketch, "E99", {"start": v(0, 209.55) * mm, "end": v(0, 220.98) * mm});
            skSolve(sketch);
        }
        {
            var Q0;
            Q0=sQuery(id+"F22.wireOp",VERTEX,"E99.end");
            var Q1;
            Q1=makeQuery(id+"F18.opPattern","COPY",BODY,{"derivedFrom":makeQuery(id+"F17.opExtrude","SWEPT_BODY",BODY,{"disambiguationData":[OSD([sQuery(id+"F16.wireOp",EDGE,"E89"),sQuery(id+"F16.wireOp",EDGE,"E90"),sQuery(id+"F16.wireOp",EDGE,"E91"),sQuery(id+"F16.wireOp",EDGE,"E92")])]}),"instanceName":"1"});
            hole(context, id + "F23", {"style" : HoleStyle.SIMPLE, "endStyle" : HoleEndStyle.THROUGH, "standardTappedOrClearance" : lookupTablePath({ "standard" : "ANSI", "fit" : "Close", "size" : "#8", "type" : "Clearance" }), "standardBlindInLast" : lookupTablePath({ "fit" : "Close", "standard" : "ANSI", "size" : "#8", "type" : "Clearance" }), "holeDiameter" : 4.32 * mm, "majorDiameter" : 6.35 * mm, "isTappedThrough" : true, "tappedDepth" : 12.7 * mm, "tapClearance" : 3, "locations" : qUnion([Q0]), "scope" : qUnion([Q1])});
        }
        {
            var Q0;
            Q0=makeQuery(id+"F13.opExtrude","CAP_EDGE",EDGE,{"disambiguationData":[OSD([sQuery(id+"F12.wireOp",EDGE,"E59.trimOffspring")])],"isStart":false});
            var Q1;
            Q1=makeQuery(id+"F13.opExtrude","CAP_EDGE",EDGE,{"disambiguationData":[OSD([sQuery(id+"F12.wireOp",EDGE,"E59.trimOffspring")])],"isStart":true});
            var Q2;
            Q2=makeQuery(id+"F17.opExtrude","CAP_EDGE",EDGE,{"disambiguationData":[OSD([sQuery(id+"F16.wireOp",EDGE,"E90")])],"isStart":false});
            var Q3;
            Q3=makeQuery(id+"F18.opPattern","COPY",EDGE,{"derivedFrom":makeQuery(id+"F17.opExtrude","CAP_EDGE",EDGE,{"disambiguationData":[OSD([sQuery(id+"F16.wireOp",EDGE,"E90")])],"isStart":false}),"instanceName":"1"});
            var Q4;
            Q4=makeQuery(id+"F17.opExtrude","SWEPT_EDGE",EDGE,{"disambiguationData":[OSD([sQuery(id+"F12.wireOp",EDGE,"E47.trimOffspring"),sQuery(id+"F16.wireOp",EDGE,"E90"),sQuery(id+"F16.wireOp",EDGE,"E91")])]});
            var Q5;
            Q5=makeQuery(id+"F18.opPattern","COPY",EDGE,{"derivedFrom":makeQuery(id+"F17.opExtrude","SWEPT_EDGE",EDGE,{"disambiguationData":[OSD([sQuery(id+"F12.wireOp",EDGE,"E47.trimOffspring"),sQuery(id+"F16.wireOp",EDGE,"E90"),sQuery(id+"F16.wireOp",EDGE,"E91")])]}),"instanceName":"1"});
            var Q6;
            Q6=makeQuery(id+"F13.opExtrude","CAP_EDGE",EDGE,{"disambiguationData":[OSD([sQuery(id+"F12.wireOp",EDGE,"E50.trimOffspring")])],"isStart":false});
            var Q7;
            Q7=makeQuery(id+"F13.opExtrude","CAP_EDGE",EDGE,{"disambiguationData":[OSD([sQuery(id+"F12.wireOp",EDGE,"E50.trimOffspring")])],"isStart":true});
            var Q8;
            Q8=makeQuery(id+"F13.opExtrude","SWEPT_EDGE",EDGE,{"disambiguationData":[OSD([sQuery(id+"F12.wireOp",EDGE,"E41"),sQuery(id+"F12.wireOp",EDGE,"E52.trimOffspring")])]});
            var Q9;
            Q9=makeQuery(id+"F13.opExtrude","CAP_EDGE",EDGE,{"disambiguationData":[OSD([sQuery(id+"F12.wireOp",EDGE,"E49.trimOffspring")])],"isStart":false});
            var Q10;
            Q10=makeQuery(id+"F13.opExtrude","CAP_EDGE",EDGE,{"disambiguationData":[OSD([sQuery(id+"F12.wireOp",EDGE,"E49.trimOffspring")])],"isStart":true});
            var Q11;
            Q11=makeQuery(id+"F13.opExtrude","CAP_EDGE",EDGE,{"disambiguationData":[OSD([sQuery(id+"F12.wireOp",EDGE,"E53.trimOffspring")])],"isStart":false});
            var Q12;
            Q12=makeQuery(id+"F13.opExtrude","CAP_EDGE",EDGE,{"disambiguationData":[OSD([sQuery(id+"F12.wireOp",EDGE,"E53.trimOffspring")])],"isStart":true});
            fillet(context, id + "F24", {"entities" : qUnion([Q0, Q1, Q2, Q3, Q4, Q5, Q6, Q7, Q8, Q9, Q10, Q11, Q12]), "radius" : 1.27 * mm, "tangentPropagation" : true, "allowEdgeOverflow" : false});
        }
        {
            var Q0;
            {var subQ0=makeQuery(id+"F17.opExtrude","SWEPT_EDGE",EDGE,{"disambiguationData":[OSD([sQuery(id+"F16.wireOp",EDGE,"E89"),sQuery(id+"F16.wireOp",EDGE,"E90")])]});Q0=makeQuery(id+"F19.opBoolean","MERGE",EDGE,{"derivedFrom":[makeQuery(id+"F13.opExtrude","SWEPT_EDGE",EDGE,{"disambiguationData":[OSD([sQuery(id+"F12.wireOp",EDGE,"E82"),sQuery(id+"F12.wireOp",EDGE,"E83")])]}),subQ0,makeQuery(id+"F18.opPattern","COPY",EDGE,{"derivedFrom":subQ0,"instanceName":"1"})]});}
            fillet(context, id + "F25", {"entities" : qUnion([Q0]), "radius" : 0.76 * mm, "tangentPropagation" : true, "allowEdgeOverflow" : false});
        }
        {
            var Q0;
            Q0=qCreatedBy(makeId("Front.planeOp"),FACE);
            cPlane(context, id + "F26", {"entities" : qUnion([Q0]), "cplaneType" : CPlaneType.OFFSET, "offset" : 76.2 * mm, "width" : 152.4 * mm, "height" : 152.4 * mm});
        }
        {
            var Q0;
            Q0=qCreatedBy(id+"F26.planeOp",FACE);
            cPlane(context, id + "F27", {"entities" : qUnion([Q0]), "cplaneType" : CPlaneType.OFFSET, "offset" : 152.4 * mm, "oppositeDirection" : true, "width" : 152.4 * mm, "height" : 152.4 * mm});
        }
        {
            var Q0;
            Q0=makeQuery(id+"F18.opPattern","COPY",BODY,{"derivedFrom":makeQuery(id+"F17.opExtrude","SWEPT_BODY",BODY,{"disambiguationData":[OSD([sQuery(id+"F16.wireOp",EDGE,"E89"),sQuery(id+"F16.wireOp",EDGE,"E90"),sQuery(id+"F16.wireOp",EDGE,"E91"),sQuery(id+"F16.wireOp",EDGE,"E92")])]}),"instanceName":"1"});
            var Q1;
            Q1=qCreatedBy(id+"F26.planeOp",FACE);
            mirror(context, id + "F28", {"entities" : qUnion([Q0]), "mirrorPlane" : qUnion([Q1])});
        }
        {
            var Q0;
            Q0=makeQuery(id+"F18.opPattern","COPY",BODY,{"derivedFrom":makeQuery(id+"F17.opExtrude","SWEPT_BODY",BODY,{"disambiguationData":[OSD([sQuery(id+"F16.wireOp",EDGE,"E89"),sQuery(id+"F16.wireOp",EDGE,"E90"),sQuery(id+"F16.wireOp",EDGE,"E91"),sQuery(id+"F16.wireOp",EDGE,"E92")])]}),"instanceName":"1"});
            var Q1;
            Q1=qCreatedBy(id+"F27.planeOp",FACE);
            mirror(context, id + "F29", {"entities" : qUnion([Q0]), "mirrorPlane" : qUnion([Q1])});
        }
        {
            var Q0;
            Q0=makeQuery(id+"F11.opExtrude","SWEPT_BODY",BODY,{"disambiguationData":[OSD([sQuery(id+"F10.wireOp",EDGE,"E35"),sQuery(id+"F10.wireOp",EDGE,"E36")])]});
            var Q1;
            Q1=makeQuery(id+"F28.opPattern","COPY",BODY,{"derivedFrom":makeQuery(id+"F18.opPattern","COPY",BODY,{"derivedFrom":makeQuery(id+"F17.opExtrude","SWEPT_BODY",BODY,{"disambiguationData":[OSD([sQuery(id+"F16.wireOp",EDGE,"E89"),sQuery(id+"F16.wireOp",EDGE,"E90"),sQuery(id+"F16.wireOp",EDGE,"E91"),sQuery(id+"F16.wireOp",EDGE,"E92")])]}),"instanceName":"1"}),"instanceName":"1"});
            var Q2;
            Q2=makeQuery(id+"F18.opPattern","COPY",BODY,{"derivedFrom":makeQuery(id+"F17.opExtrude","SWEPT_BODY",BODY,{"disambiguationData":[OSD([sQuery(id+"F16.wireOp",EDGE,"E89"),sQuery(id+"F16.wireOp",EDGE,"E90"),sQuery(id+"F16.wireOp",EDGE,"E91"),sQuery(id+"F16.wireOp",EDGE,"E92")])]}),"instanceName":"1"});
            var Q3;
            Q3=makeQuery(id+"F29.opPattern","COPY",BODY,{"derivedFrom":makeQuery(id+"F18.opPattern","COPY",BODY,{"derivedFrom":makeQuery(id+"F17.opExtrude","SWEPT_BODY",BODY,{"disambiguationData":[OSD([sQuery(id+"F16.wireOp",EDGE,"E89"),sQuery(id+"F16.wireOp",EDGE,"E90"),sQuery(id+"F16.wireOp",EDGE,"E91"),sQuery(id+"F16.wireOp",EDGE,"E92")])]}),"instanceName":"1"}),"instanceName":"1"});
            var Q4;
            Q4=qCreatedBy(makeId("Right.planeOp"),FACE);
            mirror(context, id + "F30", {"entities" : qUnion([Q0, Q1, Q2, Q3]), "mirrorPlane" : qUnion([Q4])});
        }
        {
            var Q0;
            Q0=makeQuery(id+"F29.opPattern","COPY",BODY,{"derivedFrom":makeQuery(id+"F18.opPattern","COPY",BODY,{"derivedFrom":makeQuery(id+"F17.opExtrude","SWEPT_BODY",BODY,{"disambiguationData":[OSD([sQuery(id+"F16.wireOp",EDGE,"E89"),sQuery(id+"F16.wireOp",EDGE,"E90"),sQuery(id+"F16.wireOp",EDGE,"E91"),sQuery(id+"F16.wireOp",EDGE,"E92")])]}),"instanceName":"1"}),"instanceName":"1"});
            var Q1;
            Q1=makeQuery(id+"F18.opPattern","COPY",BODY,{"derivedFrom":makeQuery(id+"F17.opExtrude","SWEPT_BODY",BODY,{"disambiguationData":[OSD([sQuery(id+"F16.wireOp",EDGE,"E89"),sQuery(id+"F16.wireOp",EDGE,"E90"),sQuery(id+"F16.wireOp",EDGE,"E91"),sQuery(id+"F16.wireOp",EDGE,"E92")])]}),"instanceName":"1"});
            var Q2;
            Q2=makeQuery(id+"F11.opExtrude","SWEPT_BODY",BODY,{"disambiguationData":[OSD([sQuery(id+"F10.wireOp",EDGE,"E35"),sQuery(id+"F10.wireOp",EDGE,"E36")])]});
            var Q3;
            Q3=makeQuery(id+"F30.opPattern","COPY",BODY,{"derivedFrom":makeQuery(id+"F29.opPattern","COPY",BODY,{"derivedFrom":makeQuery(id+"F18.opPattern","COPY",BODY,{"derivedFrom":makeQuery(id+"F17.opExtrude","SWEPT_BODY",BODY,{"disambiguationData":[OSD([sQuery(id+"F16.wireOp",EDGE,"E89"),sQuery(id+"F16.wireOp",EDGE,"E90"),sQuery(id+"F16.wireOp",EDGE,"E91"),sQuery(id+"F16.wireOp",EDGE,"E92")])]}),"instanceName":"1"}),"instanceName":"1"}),"instanceName":"1"});
            var Q4;
            Q4=makeQuery(id+"F30.opPattern","COPY",BODY,{"derivedFrom":makeQuery(id+"F11.opExtrude","SWEPT_BODY",BODY,{"disambiguationData":[OSD([sQuery(id+"F10.wireOp",EDGE,"E35"),sQuery(id+"F10.wireOp",EDGE,"E36")])]}),"instanceName":"1"});
            var Q5;
            Q5=makeQuery(id+"F30.opPattern","COPY",BODY,{"derivedFrom":makeQuery(id+"F18.opPattern","COPY",BODY,{"derivedFrom":makeQuery(id+"F17.opExtrude","SWEPT_BODY",BODY,{"disambiguationData":[OSD([sQuery(id+"F16.wireOp",EDGE,"E89"),sQuery(id+"F16.wireOp",EDGE,"E90"),sQuery(id+"F16.wireOp",EDGE,"E91"),sQuery(id+"F16.wireOp",EDGE,"E92")])]}),"instanceName":"1"}),"instanceName":"1"});
            var Q6;
            Q6=makeQuery(id+"F28.opPattern","COPY",BODY,{"derivedFrom":makeQuery(id+"F18.opPattern","COPY",BODY,{"derivedFrom":makeQuery(id+"F17.opExtrude","SWEPT_BODY",BODY,{"disambiguationData":[OSD([sQuery(id+"F16.wireOp",EDGE,"E89"),sQuery(id+"F16.wireOp",EDGE,"E90"),sQuery(id+"F16.wireOp",EDGE,"E91"),sQuery(id+"F16.wireOp",EDGE,"E92")])]}),"instanceName":"1"}),"instanceName":"1"});
            var Q7;
            Q7=makeQuery(id+"F30.opPattern","COPY",BODY,{"derivedFrom":makeQuery(id+"F28.opPattern","COPY",BODY,{"derivedFrom":makeQuery(id+"F18.opPattern","COPY",BODY,{"derivedFrom":makeQuery(id+"F17.opExtrude","SWEPT_BODY",BODY,{"disambiguationData":[OSD([sQuery(id+"F16.wireOp",EDGE,"E89"),sQuery(id+"F16.wireOp",EDGE,"E90"),sQuery(id+"F16.wireOp",EDGE,"E91"),sQuery(id+"F16.wireOp",EDGE,"E92")])]}),"instanceName":"1"}),"instanceName":"1"}),"instanceName":"1"});
            transform(context, id + "F31", {"entities" : qUnion([Q0, Q1, Q2, Q3, Q4, Q5, Q6, Q7]), "transformType" : TransformType.TRANSLATION_3D, "dx" : 0 * mm, "dy" : 0 * mm, "dz" : -76.2 * mm, "makeCopy" : false});
        }
        {
            var Q0;
            Q0=qCreatedBy(makeId("Front.planeOp"),FACE);
            var sketch = newSketch(context, id + "F32", { "sketchPlane" : qUnion([Q0])});
            skCircle(sketch, "E100", {"center": v(292.1, 203.2) * mm, "radius": 39.5 * mm});
            skLineSegment(sketch, "E101", {"start": v(292.1, 203.2) * mm, "end": v(292.1, 175.26) * mm});
            skCircle(sketch, "E102", {"center": v(292.1, 175.26) * mm, "radius": 6.35 * mm});
            skLineSegment(sketch, "E103", {"start": v(292.1, 175.26) * mm, "end": v(292.1, 181.61) * mm});
            skCircle(sketch, "E104", {"center": v(292.1, 181.61) * mm, "radius": 2.54 * mm});
            skCircle(sketch, "E105.1.0", {"center": v(286.6, 178.44) * mm, "radius": 2.54 * mm});
            skCircle(sketch, "E105.2.0", {"center": v(286.6, 172.09) * mm, "radius": 2.54 * mm});
            skCircle(sketch, "E105.3.0", {"center": v(292.1, 168.9) * mm, "radius": 2.54 * mm});
            skCircle(sketch, "E105.4.0", {"center": v(297.6, 172.09) * mm, "radius": 2.54 * mm});
            skCircle(sketch, "E105.5.0", {"center": v(297.6, 178.44) * mm, "radius": 2.54 * mm});
            skCircle(sketch, "E106", {"center": v(292.1, 175.26) * mm, "radius": 2.54 * mm});
            skSolve(sketch);
        }
        {
            var Q0;
            Q0 = qSketchRegion(id + "F32", true);
            var Q1;
            Q1=makeQuery(id+"F32.imprint","IMPRINT",FACE,{"disambiguationData":[TD([[makeQuery(id+"F32.imprint","IMPRINT",EDGE,{"derivedFrom":sQuery(id+"F32.wireOp",EDGE,"E106")}),-1.0]])]});
            extrude(context, id + "F33", {"entities" : qUnion([Q0, Q1]), "endBound" : BoundingType.SYMMETRIC, "depth" : 1.59 * mm, "offsetDistance" : 25.4 * mm});
        }
        {
            var Q0;
            Q0=qCreatedBy(makeId("Front.planeOp"),FACE);
            cPlane(context, id + "F34", {"entities" : qUnion([Q0]), "cplaneType" : CPlaneType.OFFSET, "offset" : 76.2 * mm, "width" : 152.4 * mm, "height" : 152.4 * mm});
        }
        {
            var Q0;
            Q0=qCreatedBy(makeId("Front.planeOp"),FACE);
            cPlane(context, id + "F35", {"entities" : qUnion([Q0]), "cplaneType" : CPlaneType.OFFSET, "offset" : 76.2 * mm, "oppositeDirection" : true, "width" : 152.4 * mm, "height" : 152.4 * mm});
        }
        {
            var Q0;
            Q0=makeQuery(id+"F33.opExtrude","SWEPT_BODY",BODY,{"disambiguationData":[OSD([sQuery(id+"F32.wireOp",EDGE,"E100"),sQuery(id+"F32.wireOp",EDGE,"E104"),sQuery(id+"F32.wireOp",EDGE,"E105.1.0"),sQuery(id+"F32.wireOp",EDGE,"E105.2.0"),sQuery(id+"F32.wireOp",EDGE,"E105.3.0"),sQuery(id+"F32.wireOp",EDGE,"E105.4.0"),sQuery(id+"F32.wireOp",EDGE,"E105.5.0"),sQuery(id+"F32.wireOp",EDGE,"E106")])]});
            var Q1;
            Q1=qCreatedBy(id+"F34.planeOp",FACE);
            mirror(context, id + "F36", {"entities" : qUnion([Q0]), "mirrorPlane" : qUnion([Q1])});
        }
        {
            var Q0;
            Q0=makeQuery(id+"F33.opExtrude","SWEPT_BODY",BODY,{"disambiguationData":[OSD([sQuery(id+"F32.wireOp",EDGE,"E100"),sQuery(id+"F32.wireOp",EDGE,"E104"),sQuery(id+"F32.wireOp",EDGE,"E105.1.0"),sQuery(id+"F32.wireOp",EDGE,"E105.2.0"),sQuery(id+"F32.wireOp",EDGE,"E105.3.0"),sQuery(id+"F32.wireOp",EDGE,"E105.4.0"),sQuery(id+"F32.wireOp",EDGE,"E105.5.0"),sQuery(id+"F32.wireOp",EDGE,"E106")])]});
            var Q1;
            Q1=qCreatedBy(id+"F35.planeOp",FACE);
            mirror(context, id + "F37", {"entities" : qUnion([Q0]), "mirrorPlane" : qUnion([Q1])});
        }
        {
            var Q0;
            Q0=makeQuery(id+"F33.opExtrude","SWEPT_BODY",BODY,{"disambiguationData":[OSD([sQuery(id+"F32.wireOp",EDGE,"E100"),sQuery(id+"F32.wireOp",EDGE,"E104"),sQuery(id+"F32.wireOp",EDGE,"E105.1.0"),sQuery(id+"F32.wireOp",EDGE,"E105.2.0"),sQuery(id+"F32.wireOp",EDGE,"E105.3.0"),sQuery(id+"F32.wireOp",EDGE,"E105.4.0"),sQuery(id+"F32.wireOp",EDGE,"E105.5.0"),sQuery(id+"F32.wireOp",EDGE,"E106")])]});
            var Q1;
            Q1=makeQuery(id+"F36.opPattern","COPY",BODY,{"derivedFrom":makeQuery(id+"F33.opExtrude","SWEPT_BODY",BODY,{"disambiguationData":[OSD([sQuery(id+"F32.wireOp",EDGE,"E100"),sQuery(id+"F32.wireOp",EDGE,"E104"),sQuery(id+"F32.wireOp",EDGE,"E105.1.0"),sQuery(id+"F32.wireOp",EDGE,"E105.2.0"),sQuery(id+"F32.wireOp",EDGE,"E105.3.0"),sQuery(id+"F32.wireOp",EDGE,"E105.4.0"),sQuery(id+"F32.wireOp",EDGE,"E105.5.0"),sQuery(id+"F32.wireOp",EDGE,"E106")])]}),"instanceName":"1"});
            var Q2;
            Q2=makeQuery(id+"F37.opPattern","COPY",BODY,{"derivedFrom":makeQuery(id+"F33.opExtrude","SWEPT_BODY",BODY,{"disambiguationData":[OSD([sQuery(id+"F32.wireOp",EDGE,"E100"),sQuery(id+"F32.wireOp",EDGE,"E104"),sQuery(id+"F32.wireOp",EDGE,"E105.1.0"),sQuery(id+"F32.wireOp",EDGE,"E105.2.0"),sQuery(id+"F32.wireOp",EDGE,"E105.3.0"),sQuery(id+"F32.wireOp",EDGE,"E105.4.0"),sQuery(id+"F32.wireOp",EDGE,"E105.5.0"),sQuery(id+"F32.wireOp",EDGE,"E106")])]}),"instanceName":"1"});
            var Q3;
            Q3=qCreatedBy(makeId("Right.planeOp"),FACE);
            mirror(context, id + "F38", {"entities" : qUnion([Q0, Q1, Q2]), "mirrorPlane" : qUnion([Q3])});
        }
    });
